AUTODESK INVENTOR PART (.ipt)
format: ipt  version: unknown  size: 135,168 bytes
history: native  units: mm (DEFAULTED — no unit token found)
features: plane x3, imported_body x1
ambient origin geometry x5: Origin, X Axis, Y Axis, Z Axis, Center Point
feature tree (4):
  imported_body  "Base1"
  plane  "YZ Plane (RIGHT)"
  plane  "XZ Plane (TOP)"
  plane  "XY Plane (FRONT)"
